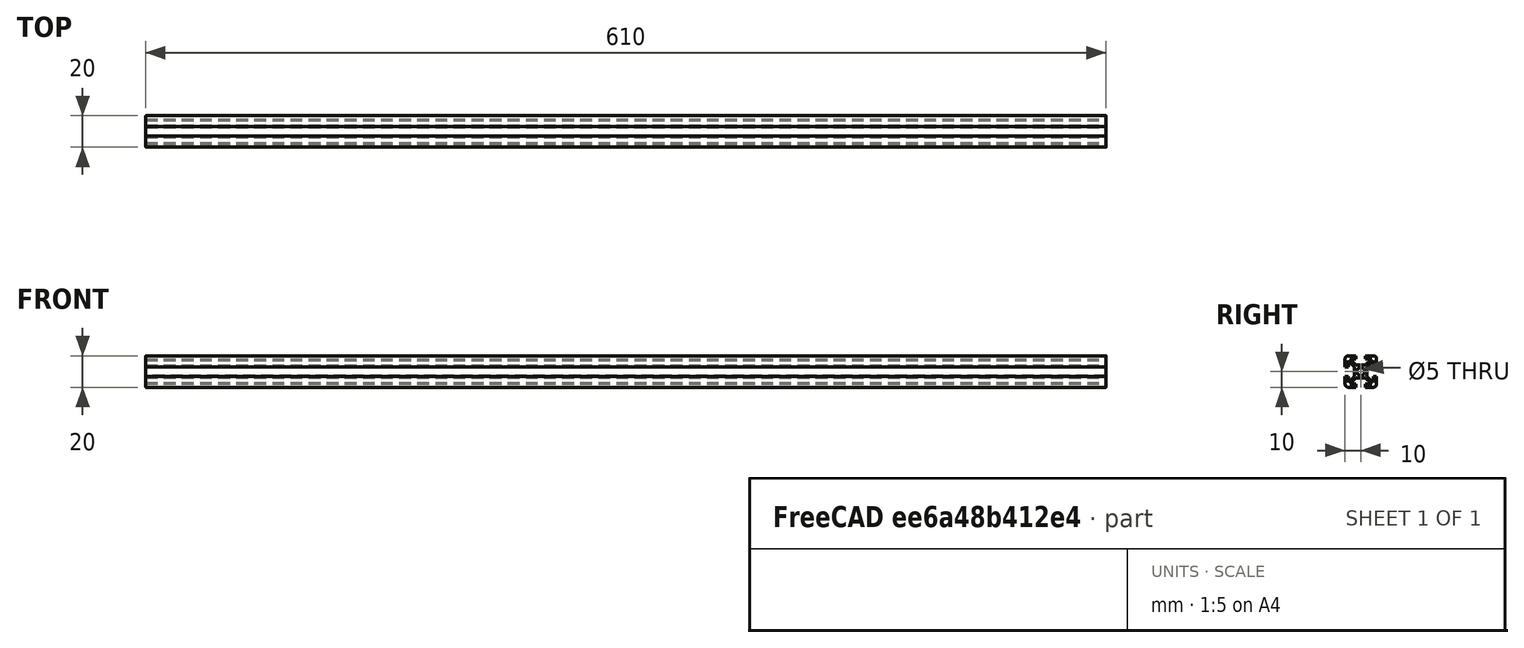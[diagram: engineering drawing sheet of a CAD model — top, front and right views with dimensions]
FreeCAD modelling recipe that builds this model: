
FCSTD DOCUMENT  (FreeCAD 0.19R24267 +99 (Git))
Label: 2020 Rail strut upright 610mm
License: All rights reserved
LicenseURL: http://en.wikipedia.org/wiki/All_rights_reserved
objects: Sketcher::SketchObject×1, PartDesign::Pad×1, PartDesign::Body×1
note: 4 computed .brp shape members not serialized (recipe doc carries the construction recipe); baked Part::Feature solids carry a one-line shape summary decoded from their .brp

FEATURE [Sketcher::SketchObject] Sketch  label="Rail cross section"
  FullyConstrained = true
  MapMode = 5
  Placement = pos=(0,0,0) rot=(0.57735,0.57735,0.57735;2.0944rad)
  Support = -> [YZ_Plane]
  sketch-geometry (47):
    g0: ArcOfCircle CenterX=-8 CenterY=8 CenterZ=0 NormalX=0 NormalY=0 NormalZ=1 AngleXU=0 Radius=2 StartAngle=1.5708 EndAngle=3.14159
    g1: ArcOfCircle CenterX=-8 CenterY=-8 CenterZ=0 NormalX=0 NormalY=0 NormalZ=1 AngleXU=0 Radius=2 StartAngle=3.14159 EndAngle=4.71239
    g2: ArcOfCircle CenterX=8 CenterY=-8 CenterZ=0 NormalX=0 NormalY=0 NormalZ=1 AngleXU=0 Radius=2 StartAngle=4.71239 EndAngle=6.28319
    g3: ArcOfCircle CenterX=8 CenterY=8 CenterZ=0 NormalX=0 NormalY=0 NormalZ=1 AngleXU=0 Radius=2 StartAngle=2e-16 EndAngle=1.5708
    g4: Circle CenterX=0 CenterY=0 CenterZ=0 NormalX=0 NormalY=0 NormalZ=1 AngleXU=0 Radius=2.5
    g5: LineSegment StartX=-10 StartY=8 StartZ=0 EndX=-10 EndY=3 EndZ=0
    g6: LineSegment StartX=-10 StartY=-3 StartZ=0 EndX=-10 EndY=-8 EndZ=0
    g7: LineSegment StartX=-8 StartY=-10 StartZ=0 EndX=-3 EndY=-10 EndZ=0
    g8: LineSegment StartX=3 StartY=-10 StartZ=0 EndX=8 EndY=-10 EndZ=0
    g9: LineSegment StartX=10 StartY=-8 StartZ=0 EndX=10 EndY=-3 EndZ=0
    g10: LineSegment StartX=10 StartY=3 StartZ=0 EndX=10 EndY=8 EndZ=0
    g11: LineSegment StartX=-8 StartY=10 StartZ=0 EndX=-3 EndY=10 EndZ=0
    g12: LineSegment StartX=3 StartY=10 StartZ=0 EndX=8 EndY=10 EndZ=0
    g13: LineSegment StartX=-3 StartY=4 StartZ=0 EndX=3 EndY=4 EndZ=0
    g14: LineSegment StartX=4 StartY=3 StartZ=0 EndX=4 EndY=-3 EndZ=0
    g15: LineSegment StartX=3 StartY=-4 StartZ=0 EndX=-3 EndY=-4 EndZ=0
    g16: LineSegment StartX=-4 StartY=-3 StartZ=0 EndX=-4 EndY=3 EndZ=0
    g17: LineSegment StartX=-3 StartY=-4 StartZ=0 EndX=-7 EndY=-8 EndZ=0
    g18: LineSegment StartX=-3 StartY=-10 StartZ=0 EndX=-3 EndY=-8 EndZ=0
    g19: LineSegment StartX=3 StartY=-4 StartZ=0 EndX=7 EndY=-8 EndZ=0
    g20: LineSegment StartX=4 StartY=-3 StartZ=0 EndX=8 EndY=-7 EndZ=0
    g21: LineSegment StartX=8 StartY=-7 StartZ=0 EndX=8 EndY=-3 EndZ=0
    g22: LineSegment StartX=10 StartY=-3 StartZ=0 EndX=8 EndY=-3 EndZ=0
    g23: LineSegment StartX=4 StartY=3 StartZ=0 EndX=8 EndY=7 EndZ=0
    g24: LineSegment StartX=8 StartY=7 StartZ=0 EndX=8 EndY=3 EndZ=0
    g25: LineSegment StartX=8 StartY=3 StartZ=0 EndX=10 EndY=3 EndZ=0
    g26: LineSegment StartX=3 StartY=10 StartZ=0 EndX=3 EndY=8 EndZ=0
    g27: LineSegment StartX=3 StartY=8 StartZ=0 EndX=7 EndY=8 EndZ=0
    g28: LineSegment StartX=7 StartY=8 StartZ=0 EndX=3 EndY=4 EndZ=0
    g29: LineSegment StartX=-3 StartY=4 StartZ=0 EndX=-7 EndY=8 EndZ=0
    g30: LineSegment StartX=-7 StartY=8 StartZ=0 EndX=-3 EndY=8 EndZ=0
    g31: LineSegment StartX=-3 StartY=8 StartZ=0 EndX=-3 EndY=10 EndZ=0
    g32: LineSegment StartX=-4 StartY=3 StartZ=0 EndX=-8 EndY=7 EndZ=0
    g33: LineSegment StartX=-8 StartY=3 StartZ=0 EndX=-10 EndY=3 EndZ=0
    g34: LineSegment StartX=-10 StartY=-3 StartZ=0 EndX=-8 EndY=-3 EndZ=0
    g35: LineSegment StartX=-8 StartY=-7 StartZ=0 EndX=-4 EndY=-3 EndZ=0
    g36: LineSegment StartX=3 StartY=-10 StartZ=0 EndX=3 EndY=-8 EndZ=0
    g37: LineSegment StartX=3 StartY=-8 StartZ=0 EndX=7 EndY=-8 EndZ=0
    g38: LineSegment StartX=-3 StartY=-8 StartZ=0 EndX=-7 EndY=-8 EndZ=0
    g39: LineSegment StartX=-8 StartY=-7 StartZ=0 EndX=-8 EndY=-3 EndZ=0
    g40: LineSegment StartX=-8 StartY=3 StartZ=0 EndX=-8 EndY=7 EndZ=0
    g41: LineSegment StartX=-3 StartY=10 StartZ=0 EndX=3 EndY=10 EndZ=0
    g42: LineSegment StartX=10 StartY=3 StartZ=0 EndX=10 EndY=-3 EndZ=0
    g43: LineSegment StartX=3 StartY=-10 StartZ=0 EndX=-3 EndY=-10 EndZ=0
    g44: LineSegment StartX=-10 StartY=-3 StartZ=0 EndX=-10 EndY=3 EndZ=0
    g45: LineSegment StartX=-4 StartY=-3 StartZ=0 EndX=-3 EndY=-4 EndZ=0
    g46: LineSegment StartX=-8 StartY=-7 StartZ=0 EndX=-7 EndY=-8 EndZ=0
  constraints (128):
    c: Radius(g0) = 2  'ASSUMED EDGE RADIUS'
    c: Equal(g1,g2)
    c: Coincident(g4,g-1)
    c: Radius(g4) = 2.5  'CENTER HOLE'
    c: Vertical(g6)
    c: Horizontal(g7)
    c: Horizontal(g8)
    c: Vertical(g9)
    c: Vertical(g10)
    c: Horizontal(g11)
    c: Horizontal(g12)
    c: DistanceX(g0,g3) = 20  'RAIL WIDTH'
    c: Vertical(g5)
    c: DistanceY(g2,g3) = 20  'RAIL HEIGHT'
    c: DistanceX(g7,g8) = 6  'SLOT WIDTH'
    c: Equal(g8,g7)
    c: Equal(g7,g6)
    c: Equal(g5,g11)
    c: Equal(g12,g10)
    c: Tangent(g12,g3) = 1.5708
    c: Tangent(g10,g3) = -1.5708
    c: Tangent(g11,g0) = 1.5708
    c: Tangent(g5,g0) = -1.5708
    c: Tangent(g6,g1) = -1.5708
    c: Tangent(g7,g1) = -1.5708
    c: Tangent(g8,g2) = -1.5708
    c: Tangent(g9,g2) = -1.5708
    c: Symmetric(g3,g2,g-1)
    c: Symmetric(g0,g3,g-2)
    c: Horizontal(g13)
    c: Vertical(g14)
    c: Vertical(g16)
    c: Horizontal(g15)
    c: Equal(g16,g15)
    c: Equal(g15,g14)
    c: Coincident(g17,g15)
    c: Coincident(g18,g7)
    c: Vertical(g18)
    c: Coincident(g19,g15)
    c: Coincident(g20,g14)
    c: Coincident(g21,g20)
    c: Vertical(g21)
    c: Coincident(g22,g9)
    c: Coincident(g22,g21)
    c: Coincident(g23,g14)
    c: Coincident(g24,g23)
    c: Vertical(g24)
    c: Coincident(g25,g24)
    c: Coincident(g25,g10)
    c: Coincident(g26,g12)
    c: Vertical(g26)
    c: Coincident(g27,g26)
    c: Horizontal(g27)
    c: Coincident(g28,g27)
    c: Coincident(g28,g13)
    c: Coincident(g29,g13)
    c: Coincident(g30,g29)
    c: Horizontal(g30)
    c: Coincident(g31,g30)
    c: Coincident(g31,g11)
    c: Coincident(g32,g16)
    c: Coincident(g33,g5)
    c: Horizontal(g33)
    c: Coincident(g34,g6)
    c: Horizontal(g34)
    c: Coincident(g35,g16)
    c: Coincident(g36,g8)
    c: Vertical(g36)
    c: Coincident(g37,g36)
    c: Coincident(g37,g19)
    c: Coincident(g38,g18)
    c: Coincident(g38,g17)
    c: Horizontal(g38)
    c: Coincident(g39,g35)
    c: Coincident(g39,g34)
    c: Vertical(g39)
    c: Coincident(g40,g33)
    c: Coincident(g40,g32)
    c: Vertical(g40)
    c: Horizontal(g37)
    c: Horizontal(g25)
    c: Horizontal(g22)
    c: Equal(g38,g37)
    c: Equal(g37,g21)
    c: Equal(g21,g24)
    c: Equal(g24,g27)
    c: Equal(g27,g30)
    c: Equal(g30,g40)
    c: Equal(g40,g39)
    c: Vertical(g31)
    c: Equal(g31,g26)
    c: Equal(g26,g25)
    c: Equal(g25,g22)
    c: Equal(g22,g36)
    c: Equal(g36,g18)
    c: Equal(g18,g34)
    c: Equal(g34,g33)
    c: Equal(g32,g29)
    c: Equal(g29,g28)
    c: Equal(g28,g23)
    c: Equal(g23,g20)
    c: Equal(g20,g19)
    c: Equal(g19,g17)
    c: Equal(g17,g35)
    c: Coincident(g41,g11)
    c: Coincident(g41,g12)
    c: Coincident(g42,g10)
    c: Coincident(g42,g9)
    c: Coincident(g43,g8)
    c: Coincident(g43,g7)
    c: Horizontal(g43)
    c: Coincident(g44,g6)
    c: Coincident(g44,g5)
    c: Vertical(g44)
    c: Horizontal(g41)
    c: DistanceY(g8,g15) = 6  'ASSUMED SLOT DEPTH'
    c: Equal(g43,g15)
    c: Equal(g16,g13)
    c: Equal(g44,g43)
    c: Equal(g43,g42)
    c: Equal(g42,g41)
    c: Vertical(g42)
    c: DistanceY(g36,g36) = 2  'ASSUMED WALL THICKNESS'
    c: Coincident(g45,g16)
    c: Coincident(g45,g15)
    c: Coincident(g46,g35)
    c: Coincident(g46,g17)
    c: Equal(g45,g46)
FEATURE [PartDesign::Pad] Pad  label="Length"
  Direction = (1,1,1)
  Length = 610
  Length2 = 100
  Placement = pos=(0,0,0) rot=(0.57735,0.57735,0.57735;2.0944rad)
  Profile = -> Sketch
  Type = 0
FEATURE [PartDesign::Body] Body
  Group = -> [Sketch,Pad]
  Origin = -> Origin
  Tip = -> Pad
